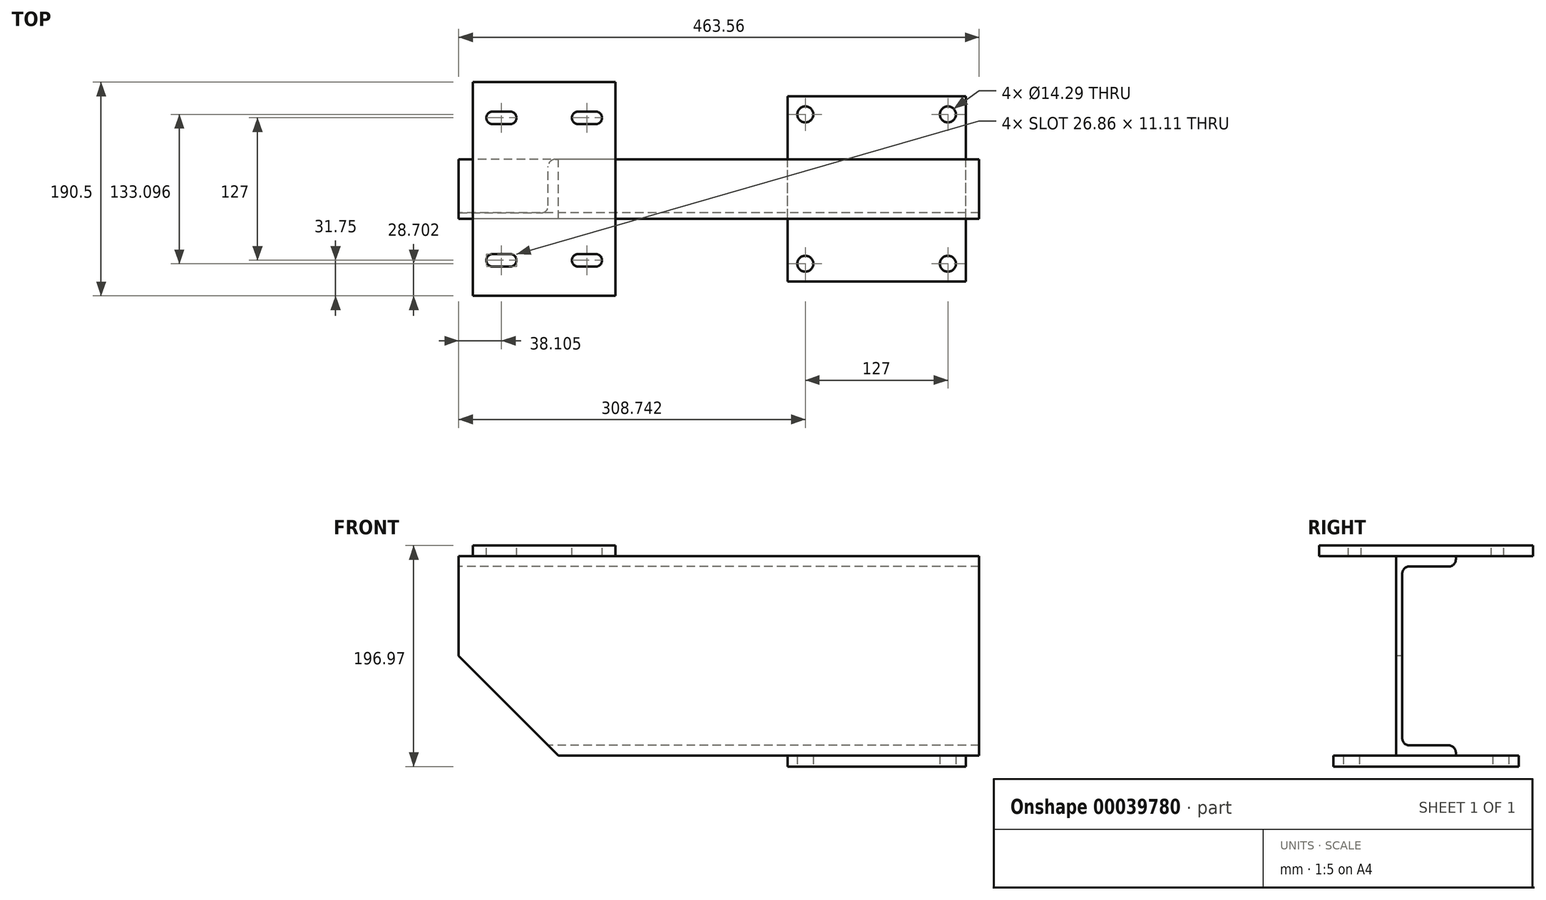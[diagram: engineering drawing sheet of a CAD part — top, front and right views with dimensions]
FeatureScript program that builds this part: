
annotation { "Feature Type Name" : "Feature", "Feature Type Description" : "" }
export const myFeature = defineFeature(function(context is Context, id is Id, definition is map)
    precondition{}
    {
        {
            var Q0;
            Q0=qCreatedBy(makeId("Right.planeOp"),FACE);
            var sketch = newSketch(context, id + "F0", { "sketchPlane" : qUnion([Q0])});
            skLineSegment(sketch, "E0", {"start": v(-57.59, 0) * mm, "end": v(57.95, 0) * mm});
            skLineSegment(sketch, "E1.0", {"start": v(-57.59, 177.8) * mm, "end": v(57.95, 177.8) * mm});
            skLineSegment(sketch, "E2", {"start": v(0, 0) * mm, "end": v(0, 9.14) * mm});
            skLineSegment(sketch, "E3.0", {"start": v(-26.54, 0) * mm, "end": v(-26.54, 177.8) * mm});
            skLineSegment(sketch, "E4.MirrorCS", {"start": v(26.54, 0) * mm, "end": v(26.54, 2.8) * mm});
            skLineSegment(sketch, "E5.0", {"start": v(-21.2, 15.5) * mm, "end": v(-21.2, 162.3) * mm});
            skLineSegment(sketch, "E6.0", {"start": v(-14.86, 9.14) * mm, "end": v(20.2, 9.14) * mm});
            skLineSegment(sketch, "E7.0", {"start": v(-14.86, 168.66) * mm, "end": v(20.2, 168.66) * mm});
            skLineSegment(sketch, "E8.trimOffspring", {"start": v(26.54, 175) * mm, "end": v(26.54, 177.8) * mm});
            skLineSegment(sketch, "E9.trimOffspring", {"start": v(0, 168.66) * mm, "end": v(0, 177.8) * mm});
            skArc(sketch, "E10.filletArc", {"start": v(-14.86, 168.66) * mm, "mid": v(-19.35, 166.8) * mm, "end": v(-21.2, 162.3) * mm});
            skArc(sketch, "E11.filletArc", {"start": v(-21.2, 15.5) * mm, "mid": v(-19.35, 11) * mm, "end": v(-14.86, 9.14) * mm});
            skArc(sketch, "E12.filletArc", {"start": v(26.54, 2.8) * mm, "mid": v(24.68, 7.28) * mm, "end": v(20.2, 9.14) * mm});
            skArc(sketch, "E13.filletArc", {"start": v(20.2, 168.66) * mm, "mid": v(24.68, 170.52) * mm, "end": v(26.54, 175) * mm});
            skSolve(sketch);
        }
        {
            var Q0;
            Q0 = qSketchRegion(id + "F0", true);
            extrude(context, id + "F1", {"entities" : qUnion([Q0]), "endBound" : BoundingType.SYMMETRIC, "depth" : 463.55 * mm});
        }
        {
            var Q0;
            Q0=makeQuery(id+"F1.opExtrude","CAP_FACE",FACE,{"disambiguationData":[OSD([sQuery(id+"F0.wireOp",EDGE,"E0"),sQuery(id+"F0.wireOp",EDGE,"E1.0"),sQuery(id+"F0.wireOp",EDGE,"E3.0"),sQuery(id+"F0.wireOp",EDGE,"E4.MirrorCS"),sQuery(id+"F0.wireOp",EDGE,"E5.0"),sQuery(id+"F0.wireOp",EDGE,"E6.0"),sQuery(id+"F0.wireOp",EDGE,"E7.0"),sQuery(id+"F0.wireOp",EDGE,"E8.trimOffspring"),sQuery(id+"F0.wireOp",EDGE,"E10.filletArc"),sQuery(id+"F0.wireOp",EDGE,"E11.filletArc"),sQuery(id+"F0.wireOp",EDGE,"E12.filletArc"),sQuery(id+"F0.wireOp",EDGE,"E13.filletArc")])],"isStart":false});
            cPlane(context, id + "F2", {"entities" : qUnion([Q0]), "cplaneType" : CPlaneType.OFFSET, "offset" : 11.94 * mm, "oppositeDirection" : true, "width" : 152.4 * mm, "height" : 152.4 * mm});
        }
        {
            var Q0;
            Q0=qCreatedBy(id+"F2.planeOp",FACE);
            var sketch = newSketch(context, id + "F3", { "sketchPlane" : qUnion([Q0])});
            skLineSegment(sketch, "E14", {"start": v(0, 0) * mm, "end": v(0, -35.2) * mm, "construction": true});
            skLineSegment(sketch, "E15.0", {"start": v(-26.54, 0) * mm, "end": v(26.54, 0) * mm, "construction": true});
            skLineSegment(sketch, "E16.0", {"start": v(-82.55, 0) * mm, "end": v(-82.55, -35.2) * mm, "construction": true});
            skLineSegment(sketch, "E17.bottom", {"start": v(-82.55, 0) * mm, "end": v(82.55, 0) * mm});
            skLineSegment(sketch, "E17.top", {"start": v(-82.55, -9.65) * mm, "end": v(82.55, -9.65) * mm});
            skLineSegment(sketch, "E17.left", {"start": v(-82.55, 0) * mm, "end": v(-82.55, -9.65) * mm});
            skLineSegment(sketch, "E17.right", {"start": v(82.55, 0) * mm, "end": v(82.55, -9.65) * mm});
            skSolve(sketch);
        }
        {
            var Q0;
            Q0 = qSketchRegion(id + "F3", true);
            extrude(context, id + "F4", {"entities" : qUnion([Q0]), "operationType" : NewBodyOperationType.ADD, "oppositeDirection" : true, "depth" : 158.75 * mm});
        }
        {
            var Q0;
            Q0=makeQuery(id+"F4.opExtrude","SWEPT_FACE",FACE,{"disambiguationData":[OSD([sQuery(id+"F3.wireOp",EDGE,"E17.top")])]});
            var sketch = newSketch(context, id + "F5", { "sketchPlane" : qUnion([Q0])});
            skLineSegment(sketch, "E18", {"start": v(140.46, 82.55) * mm, "end": v(140.46, -82.55) * mm, "construction": true});
            skLineSegment(sketch, "E19", {"start": v(219.84, 0) * mm, "end": v(61.09, 0) * mm, "construction": true});
            skLineSegment(sketch, "E20.0", {"start": v(76.96, 82.55) * mm, "end": v(76.96, -82.55) * mm, "construction": true});
            skLineSegment(sketch, "E21.0", {"start": v(219.84, 66.55) * mm, "end": v(61.09, 66.55) * mm, "construction": true});
            skPoint(sketch, "E22", {"position": v(76.96, 66.55) * mm});
            skPoint(sketch, "E23.MirrorP", {"position": v(76.96, -66.55) * mm});
            skPoint(sketch, "E24.MirrorP", {"position": v(203.96, -66.55) * mm});
            skPoint(sketch, "E25.MirrorP", {"position": v(203.96, 66.55) * mm});
            skSolve(sketch);
        }
        {
            var Q0;
            Q0=sQuery(id+"F5.wireOp",VERTEX,"E24.MirrorP");
            var Q1;
            Q1=sQuery(id+"F5.wireOp",VERTEX,"E23.MirrorP");
            var Q2;
            Q2=sQuery(id+"F5.wireOp",VERTEX,"E25.MirrorP");
            var Q3;
            Q3=sQuery(id+"F5.wireOp",VERTEX,"E22");
            var Q4;
            Q4=makeQuery(id+"F1.opExtrude","SWEPT_BODY",BODY,{"disambiguationData":[OSD([sQuery(id+"F0.wireOp",EDGE,"E0"),sQuery(id+"F0.wireOp",EDGE,"E1.0"),sQuery(id+"F0.wireOp",EDGE,"E3.0"),sQuery(id+"F0.wireOp",EDGE,"E4.MirrorCS"),sQuery(id+"F0.wireOp",EDGE,"E5.0"),sQuery(id+"F0.wireOp",EDGE,"E6.0"),sQuery(id+"F0.wireOp",EDGE,"E7.0"),sQuery(id+"F0.wireOp",EDGE,"E8.trimOffspring"),sQuery(id+"F0.wireOp",EDGE,"E10.filletArc"),sQuery(id+"F0.wireOp",EDGE,"E11.filletArc"),sQuery(id+"F0.wireOp",EDGE,"E12.filletArc"),sQuery(id+"F0.wireOp",EDGE,"E13.filletArc")])]});
            hole(context, id + "F6", {"style" : HoleStyle.SIMPLE, "holeDiameter" : 14.29 * mm, "endStyle" : HoleEndStyle.THROUGH, "locations" : qUnion([Q0, Q1, Q2, Q3]), "scope" : qUnion([Q4])});
        }
        {
            var Q0;
            Q0=makeQuery(id+"F1.opExtrude","CAP_FACE",FACE,{"disambiguationData":[OSD([sQuery(id+"F0.wireOp",EDGE,"E0"),sQuery(id+"F0.wireOp",EDGE,"E1.0"),sQuery(id+"F0.wireOp",EDGE,"E3.0"),sQuery(id+"F0.wireOp",EDGE,"E4.MirrorCS"),sQuery(id+"F0.wireOp",EDGE,"E5.0"),sQuery(id+"F0.wireOp",EDGE,"E6.0"),sQuery(id+"F0.wireOp",EDGE,"E7.0"),sQuery(id+"F0.wireOp",EDGE,"E8.trimOffspring"),sQuery(id+"F0.wireOp",EDGE,"E10.filletArc"),sQuery(id+"F0.wireOp",EDGE,"E11.filletArc"),sQuery(id+"F0.wireOp",EDGE,"E12.filletArc"),sQuery(id+"F0.wireOp",EDGE,"E13.filletArc")])],"isStart":true});
            cPlane(context, id + "F7", {"entities" : qUnion([Q0]), "cplaneType" : CPlaneType.OFFSET, "offset" : 76.2 * mm, "oppositeDirection" : true, "width" : 152.4 * mm, "height" : 152.4 * mm});
        }
        {
            var Q0;
            Q0=qCreatedBy(id+"F7.planeOp",FACE);
            var sketch = newSketch(context, id + "F8", { "sketchPlane" : qUnion([Q0])});
            skLineSegment(sketch, "E26.0", {"start": v(26.54, 177.8) * mm, "end": v(-95.25, 177.8) * mm});
            skLineSegment(sketch, "E27", {"start": v(0, 0) * mm, "end": v(0, 212.9) * mm, "construction": true});
            skLineSegment(sketch, "E28.0", {"start": v(-95.25, 0) * mm, "end": v(-95.25, 212.9) * mm, "construction": true});
            skPoint(sketch, "E29.orphan", {"position": v(-26.54, 177.8) * mm});
            skLineSegment(sketch, "E30.bottom", {"start": v(-95.25, 177.8) * mm, "end": v(95.25, 177.8) * mm});
            skLineSegment(sketch, "E30.top", {"start": v(-95.25, 187.32) * mm, "end": v(95.25, 187.32) * mm});
            skLineSegment(sketch, "E30.left", {"start": v(-95.25, 177.8) * mm, "end": v(-95.25, 187.32) * mm});
            skLineSegment(sketch, "E30.right", {"start": v(95.25, 177.8) * mm, "end": v(95.25, 187.32) * mm});
            skSolve(sketch);
        }
        {
            var Q0;
            Q0 = qSketchRegion(id + "F8", true);
            extrude(context, id + "F9", {"entities" : qUnion([Q0]), "operationType" : NewBodyOperationType.ADD, "endBound" : BoundingType.SYMMETRIC, "depth" : 127 * mm});
        }
        {
            var Q0;
            Q0=makeQuery(id+"F9.opExtrude","SWEPT_FACE",FACE,{"disambiguationData":[OSD([sQuery(id+"F8.wireOp",EDGE,"E30.top")])]});
            var sketch = newSketch(context, id + "F10", { "sketchPlane" : qUnion([Q0])});
            skLineSegment(sketch, "E31", {"start": v(-155.58, 95.25) * mm, "end": v(-155.58, -95.25) * mm, "construction": true});
            skLineSegment(sketch, "E32", {"start": v(-219.08, 0) * mm, "end": v(-92.08, 0) * mm, "construction": true});
            skLineSegment(sketch, "E33.0", {"start": v(-193.68, 95.25) * mm, "end": v(-193.68, -95.25) * mm, "construction": true});
            skLineSegment(sketch, "E34", {"start": v(-185.8, -63.5) * mm, "end": v(-201.55, -63.5) * mm});
            skArc(sketch, "E35.0.startCap", {"start": v(-185.8, -57.94) * mm, "mid": v(-180.24, -63.5) * mm, "end": v(-185.8, -69.06) * mm});
            skArc(sketch, "E35.0.endCap", {"start": v(-201.55, -69.06) * mm, "mid": v(-207.1, -63.5) * mm, "end": v(-201.55, -57.94) * mm});
            skLineSegment(sketch, "E35.0.left", {"start": v(-185.8, -69.06) * mm, "end": v(-201.55, -69.06) * mm});
            skLineSegment(sketch, "E35.0.right", {"start": v(-185.8, -57.94) * mm, "end": v(-201.55, -57.94) * mm});
            skLineSegment(sketch, "E36.MirrorCS", {"start": v(-125.35, -57.94) * mm, "end": v(-109.6, -57.94) * mm});
            skLineSegment(sketch, "E37.MirrorCS", {"start": v(-125.35, -63.5) * mm, "end": v(-109.6, -63.5) * mm});
            skLineSegment(sketch, "E38.MirrorCS", {"start": v(-125.35, -69.06) * mm, "end": v(-109.6, -69.06) * mm});
            skArc(sketch, "E39.MirrorCS", {"start": v(-125.35, -57.94) * mm, "mid": v(-130.9, -63.5) * mm, "end": v(-125.35, -69.06) * mm});
            skArc(sketch, "E40.MirrorCS", {"start": v(-109.6, -69.06) * mm, "mid": v(-104.04, -63.5) * mm, "end": v(-109.6, -57.94) * mm});
            skArc(sketch, "E41.MirrorCS", {"start": v(-201.55, 69.06) * mm, "mid": v(-207.1, 63.5) * mm, "end": v(-201.55, 57.94) * mm});
            skLineSegment(sketch, "E42.MirrorCS", {"start": v(-185.8, 69.06) * mm, "end": v(-201.55, 69.06) * mm});
            skLineSegment(sketch, "E43.MirrorCS", {"start": v(-185.8, 63.5) * mm, "end": v(-201.55, 63.5) * mm});
            skArc(sketch, "E44.MirrorCS", {"start": v(-185.8, 57.94) * mm, "mid": v(-180.24, 63.5) * mm, "end": v(-185.8, 69.06) * mm});
            skLineSegment(sketch, "E45.MirrorCS", {"start": v(-185.8, 57.94) * mm, "end": v(-201.55, 57.94) * mm});
            skArc(sketch, "E46.MirrorCS", {"start": v(-125.35, 57.94) * mm, "mid": v(-130.9, 63.5) * mm, "end": v(-125.35, 69.06) * mm});
            skArc(sketch, "E47.MirrorCS", {"start": v(-109.6, 69.06) * mm, "mid": v(-104.04, 63.5) * mm, "end": v(-109.6, 57.94) * mm});
            skLineSegment(sketch, "E48.MirrorCS", {"start": v(-125.35, 63.5) * mm, "end": v(-109.6, 63.5) * mm});
            skLineSegment(sketch, "E49.MirrorCS", {"start": v(-125.35, 57.94) * mm, "end": v(-109.6, 57.94) * mm});
            skLineSegment(sketch, "E50.MirrorCS", {"start": v(-125.35, 69.06) * mm, "end": v(-109.6, 69.06) * mm});
            skSolve(sketch);
        }
        {
            var Q0;
            Q0 = qSketchRegion(id + "F10", true);
            extrude(context, id + "F11", {"entities" : qUnion([Q0]), "operationType" : NewBodyOperationType.REMOVE, "endBound" : BoundingType.THROUGH_ALL, "oppositeDirection" : true, "depth" : 25.4 * mm});
        }
        {
            var Q0;
            Q0=makeQuery(id+"F1.opExtrude","CAP_EDGE",EDGE,{"disambiguationData":[OSD([sQuery(id+"F0.wireOp",EDGE,"E0")])],"isStart":true});
            chamfer(context, id + "F12", {"entities" : qUnion([Q0]), "width" : 88.9 * mm, "tangentPropagation" : true});
        }
    });
